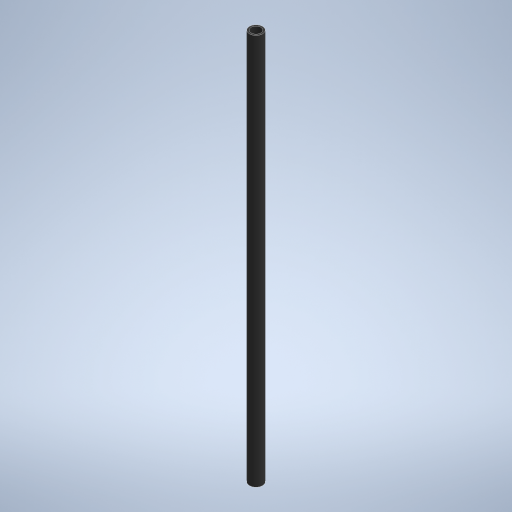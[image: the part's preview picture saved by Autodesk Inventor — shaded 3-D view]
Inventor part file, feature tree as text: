
AUTODESK INVENTOR PART (.ipt)
format: ipt  version: 2024.3 (Build 283343000, 343)  size: 240,128 bytes
history: native  units: in
note: dims shown in document units (in); Inventor stores cm internally (conversion verified against a paired STEP export)
features: extrude x1, sketch x1
ambient origin geometry x8: Origin, YZ Plane, XZ Plane, XY Plane, X Axis, Y Axis, Z Axis, Center Point
bodies: Solid1 (feature_tree)
feature tree (2):
  extrude  "Extrusion1"  Depth=4.7244in
  sketch  "Sketch1"  dims[d0=0.1181in d1=0.1575in d2=4.7244in d3=0.0in]
